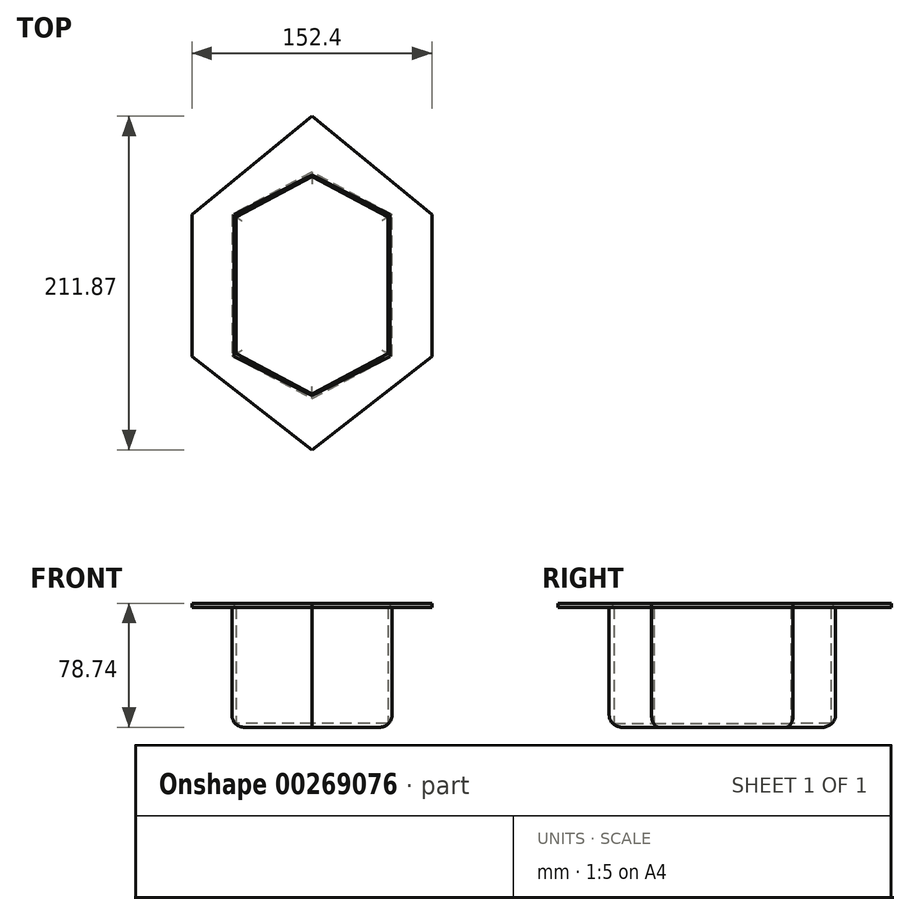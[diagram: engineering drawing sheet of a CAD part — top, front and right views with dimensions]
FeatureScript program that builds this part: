
annotation { "Feature Type Name" : "Feature", "Feature Type Description" : "" }
export const myFeature = defineFeature(function(context is Context, id is Id, definition is map)
    precondition{}
    {
        {
            var Q0;
            Q0=qCreatedBy(makeId("Top.planeOp"),FACE);
            var sketch = newSketch(context, id + "F0", { "sketchPlane" : qUnion([Q0])});
            skLineSegment(sketch, "E0", {"start": v(0, 74.58) * mm, "end": v(0, -69.14) * mm});
            skLineSegment(sketch, "E1", {"start": v(0, -69.14) * mm, "end": v(50.8, -42.23) * mm});
            skLineSegment(sketch, "E2", {"start": v(50.8, -42.23) * mm, "end": v(50.8, 47.67) * mm});
            skLineSegment(sketch, "E3", {"start": v(50.8, 47.67) * mm, "end": v(0, 74.58) * mm});
            skLineSegment(sketch, "E4", {"start": v(0, 74.58) * mm, "end": v(-50.8, 47.67) * mm});
            skLineSegment(sketch, "E5", {"start": v(-50.8, 47.67) * mm, "end": v(-50.8, -42.23) * mm});
            skLineSegment(sketch, "E6", {"start": v(-50.8, -42.23) * mm, "end": v(0, -69.14) * mm});
            skSolve(sketch);
        }
        {
            var Q0;
            Q0=makeQuery(id+"F0.imprint","IMPRINT",FACE,{"disambiguationData":[TD([[makeQuery(id+"F0.imprint","IMPRINT",EDGE,{"derivedFrom":sQuery(id+"F0.wireOp",EDGE,"E0")}),-1.0]])]});
            var Q1;
            Q1=makeQuery(id+"F0.imprint","IMPRINT",FACE,{"disambiguationData":[TD([[makeQuery(id+"F0.imprint","IMPRINT",EDGE,{"derivedFrom":sQuery(id+"F0.wireOp",EDGE,"E0")}),1.0]])]});
            extrude(context, id + "F1", {"entities" : qUnion([Q0, Q1]), "depth" : 76.2 * mm});
        }
        {
            var Q0;
            Q0=qCreatedBy(makeId("Top.planeOp"),FACE);
            cPlane(context, id + "F2", {"entities" : qUnion([Q0]), "cplaneType" : CPlaneType.OFFSET, "offset" : 76.2 * mm, "width" : 152.4 * mm, "height" : 152.4 * mm});
        }
        {
            var Q0;
            Q0=qCreatedBy(id+"F2.planeOp",FACE);
            var sketch = newSketch(context, id + "F3", { "sketchPlane" : qUnion([Q0])});
            skLineSegment(sketch, "E7", {"start": v(0, 72.87) * mm, "end": v(-49.57, 47.56) * mm});
            skLineSegment(sketch, "E8", {"start": v(-49.57, 47.56) * mm, "end": v(-49.57, -42.4) * mm});
            skLineSegment(sketch, "E9", {"start": v(-49.57, -42.4) * mm, "end": v(0, -67.1) * mm});
            skLineSegment(sketch, "E10", {"start": v(0, -67.1) * mm, "end": v(49.65, -42.4) * mm});
            skLineSegment(sketch, "E11", {"start": v(49.65, -42.4) * mm, "end": v(49.65, 47.56) * mm});
            skLineSegment(sketch, "E12", {"start": v(49.65, 47.56) * mm, "end": v(0, 72.87) * mm});
            skLineSegment(sketch, "E13", {"start": v(0, 72.87) * mm, "end": v(0, 110.13) * mm});
            skLineSegment(sketch, "E14", {"start": v(0, 110.13) * mm, "end": v(-76.2, 47.56) * mm});
            skLineSegment(sketch, "E15", {"start": v(-76.2, 47.56) * mm, "end": v(-76.2, -42.4) * mm});
            skLineSegment(sketch, "E16", {"start": v(-76.2, -42.4) * mm, "end": v(0, -101.74) * mm});
            skLineSegment(sketch, "E17", {"start": v(0, -101.74) * mm, "end": v(76.2, -42.4) * mm});
            skLineSegment(sketch, "E18", {"start": v(76.2, -42.4) * mm, "end": v(76.2, 47.56) * mm});
            skLineSegment(sketch, "E19", {"start": v(76.2, 47.56) * mm, "end": v(0, 110.13) * mm});
            skSolve(sketch);
        }
        {
            var Q0;
            Q0=makeQuery(id+"F3.imprint","IMPRINT",FACE,{"disambiguationData":[TD([[makeQuery(id+"F3.imprint","IMPRINT",EDGE,{"derivedFrom":sQuery(id+"F3.wireOp",EDGE,"E7")}),-1.0]])]});
            extrude(context, id + "F4", {"entities" : qUnion([Q0]), "operationType" : NewBodyOperationType.ADD, "depth" : 2.54 * mm});
        }
        {
            var Q0;
            Q0=makeQuery(id+"F1.opExtrude","CAP_FACE",FACE,{"disambiguationData":[OSD([sQuery(id+"F0.wireOp",EDGE,"E1"),sQuery(id+"F0.wireOp",EDGE,"E2"),sQuery(id+"F0.wireOp",EDGE,"E3"),sQuery(id+"F0.wireOp",EDGE,"E4"),sQuery(id+"F0.wireOp",EDGE,"E5"),sQuery(id+"F0.wireOp",EDGE,"E6")])],"isStart":false});
            shell(context, id + "F5", {"entities" : qUnion([Q0]), "thickness" : 2.54 * mm});
        }
        {
            var Q0;
            Q0=makeQuery(id+"F1.opExtrude","CAP_FACE",FACE,{"disambiguationData":[OSD([sQuery(id+"F0.wireOp",EDGE,"E1"),sQuery(id+"F0.wireOp",EDGE,"E2"),sQuery(id+"F0.wireOp",EDGE,"E3"),sQuery(id+"F0.wireOp",EDGE,"E4"),sQuery(id+"F0.wireOp",EDGE,"E5"),sQuery(id+"F0.wireOp",EDGE,"E6")])],"isStart":true});
            fillet(context, id + "F6", {"entities" : qUnion([Q0]), "radius" : 7.62 * mm, "tangentPropagation" : true, "allowEdgeOverflow" : false});
        }
    });
